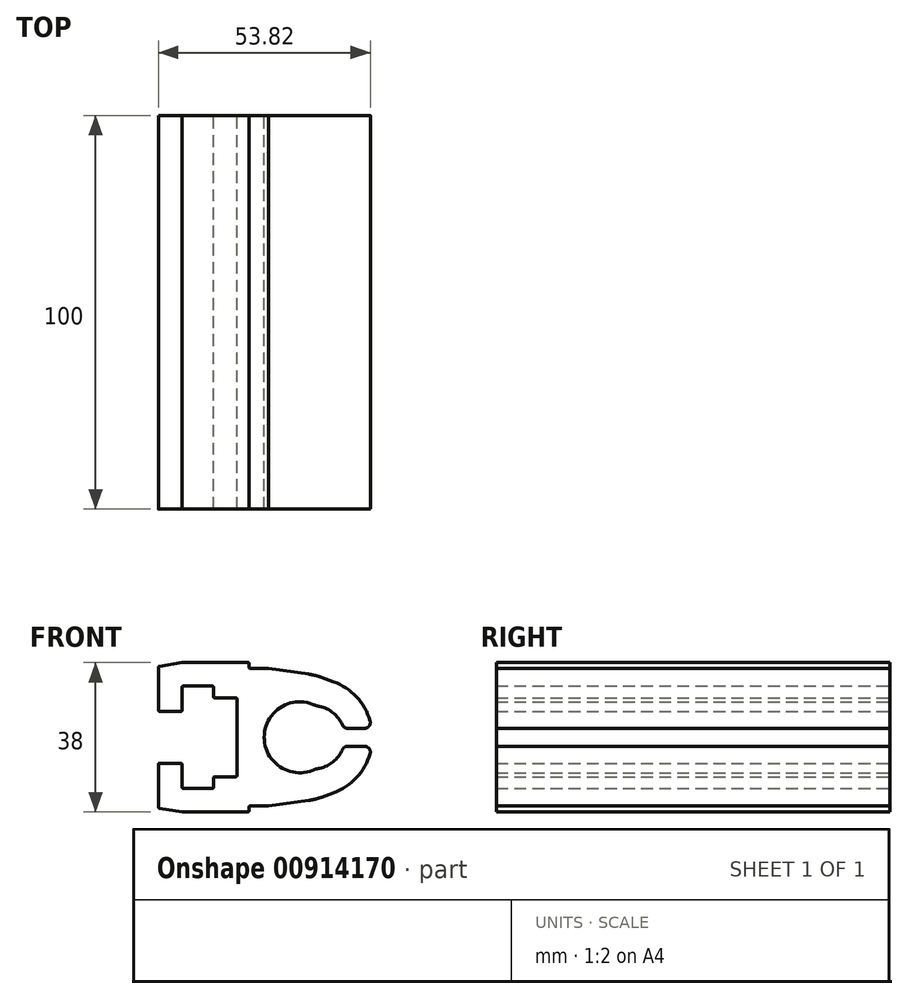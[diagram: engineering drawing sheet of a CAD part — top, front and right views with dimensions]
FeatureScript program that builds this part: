
annotation { "Feature Type Name" : "Feature", "Feature Type Description" : "" }
export const myFeature = defineFeature(function(context is Context, id is Id, definition is map)
    precondition{}
    {
        {
            var Q0;
            Q0=qCreatedBy(makeId("Front.planeOp"),FACE);
            var sketch = newSketch(context, id + "F0", { "sketchPlane" : qUnion([Q0])});
            skLineSegment(sketch, "E0", {"start": v(57.08, -14.1) * mm, "end": v(54, -15.22) * mm});
            skArc(sketch, "E1", {"start": v(50.71, -16.04) * mm, "mid": v(52.37, -15.72) * mm, "end": v(54, -15.22) * mm});
            skLineSegment(sketch, "E2", {"start": v(50.71, -16.04) * mm, "end": v(40.59, -17.47) * mm});
            skLineSegment(sketch, "E3", {"start": v(40.59, -17.47) * mm, "end": v(35.89, -17.47) * mm});
            skArc(sketch, "E4", {"start": v(35.89, -17.47) * mm, "mid": v(35.67, -17.55) * mm, "end": v(35.59, -17.77) * mm});
            skLineSegment(sketch, "E5", {"start": v(35.59, -17.77) * mm, "end": v(35.59, -18.7) * mm});
            skArc(sketch, "E6", {"start": v(35.29, -19) * mm, "mid": v(35.5, -18.91) * mm, "end": v(35.59, -18.7) * mm});
            skLineSegment(sketch, "E7", {"start": v(35.29, -19) * mm, "end": v(18.59, -19) * mm});
            skLineSegment(sketch, "E8", {"start": v(18.59, -19) * mm, "end": v(12.84, -18.04) * mm});
            skArc(sketch, "E9", {"start": v(12.59, -17.75) * mm, "mid": v(12.66, -17.94) * mm, "end": v(12.84, -18.04) * mm});
            skLineSegment(sketch, "E10", {"start": v(12.59, -17.75) * mm, "end": v(12.59, -6.87) * mm});
            skArc(sketch, "E11", {"start": v(12.89, -6.58) * mm, "mid": v(12.67, -6.66) * mm, "end": v(12.59, -6.88) * mm});
            skLineSegment(sketch, "E12", {"start": v(12.89, -6.58) * mm, "end": v(18.29, -6.58) * mm});
            skArc(sketch, "E13", {"start": v(18.59, -6.88) * mm, "mid": v(18.5, -6.66) * mm, "end": v(18.29, -6.58) * mm});
            skLineSegment(sketch, "E14", {"start": v(18.59, -6.88) * mm, "end": v(18.59, -12.7) * mm});
            skArc(sketch, "E15", {"start": v(18.59, -12.7) * mm, "mid": v(18.67, -12.91) * mm, "end": v(18.89, -13) * mm});
            skLineSegment(sketch, "E16", {"start": v(18.89, -13) * mm, "end": v(26.29, -13) * mm});
            skArc(sketch, "E17", {"start": v(26.29, -13) * mm, "mid": v(26.5, -12.91) * mm, "end": v(26.59, -12.7) * mm});
            skLineSegment(sketch, "E18", {"start": v(26.59, -12.7) * mm, "end": v(26.59, -10.3) * mm});
            skArc(sketch, "E19", {"start": v(26.89, -10) * mm, "mid": v(26.67, -10.09) * mm, "end": v(26.59, -10.3) * mm});
            skLineSegment(sketch, "E20", {"start": v(26.89, -10) * mm, "end": v(32.29, -10) * mm});
            skArc(sketch, "E21", {"start": v(32.29, -10) * mm, "mid": v(32.5, -9.91) * mm, "end": v(32.59, -9.7) * mm});
            skLineSegment(sketch, "E22", {"start": v(32.59, -9.7) * mm, "end": v(32.59, 9.7) * mm});
            skArc(sketch, "E23", {"start": v(32.59, 9.7) * mm, "mid": v(32.5, 9.91) * mm, "end": v(32.29, 10) * mm});
            skLineSegment(sketch, "E24", {"start": v(32.29, 10) * mm, "end": v(26.89, 10) * mm});
            skArc(sketch, "E25", {"start": v(26.59, 10.3) * mm, "mid": v(26.67, 10.09) * mm, "end": v(26.89, 10) * mm});
            skLineSegment(sketch, "E26", {"start": v(26.59, 10.3) * mm, "end": v(26.59, 12.7) * mm});
            skArc(sketch, "E27", {"start": v(26.59, 12.7) * mm, "mid": v(26.5, 12.91) * mm, "end": v(26.29, 13) * mm});
            skLineSegment(sketch, "E28", {"start": v(26.29, 13) * mm, "end": v(18.89, 13) * mm});
            skArc(sketch, "E29", {"start": v(18.89, 13) * mm, "mid": v(18.67, 12.91) * mm, "end": v(18.59, 12.7) * mm});
            skLineSegment(sketch, "E30", {"start": v(18.59, 12.7) * mm, "end": v(18.59, 6.88) * mm});
            skArc(sketch, "E31", {"start": v(18.29, 6.58) * mm, "mid": v(18.5, 6.66) * mm, "end": v(18.59, 6.88) * mm});
            skLineSegment(sketch, "E32", {"start": v(18.29, 6.57) * mm, "end": v(12.89, 6.57) * mm});
            skArc(sketch, "E33", {"start": v(12.59, 6.88) * mm, "mid": v(12.67, 6.66) * mm, "end": v(12.89, 6.58) * mm});
            skLineSegment(sketch, "E34", {"start": v(12.59, 6.88) * mm, "end": v(12.59, 17.75) * mm});
            skArc(sketch, "E35", {"start": v(12.84, 18.04) * mm, "mid": v(12.66, 17.94) * mm, "end": v(12.59, 17.75) * mm});
            skLineSegment(sketch, "E36", {"start": v(12.84, 18.04) * mm, "end": v(18.59, 19) * mm});
            skLineSegment(sketch, "E37", {"start": v(18.59, 19) * mm, "end": v(35.29, 19) * mm});
            skArc(sketch, "E38", {"start": v(35.59, 18.7) * mm, "mid": v(35.5, 18.91) * mm, "end": v(35.29, 19) * mm});
            skLineSegment(sketch, "E39", {"start": v(35.59, 18.7) * mm, "end": v(35.59, 17.76) * mm});
            skArc(sketch, "E40", {"start": v(35.59, 17.76) * mm, "mid": v(35.67, 17.55) * mm, "end": v(35.89, 17.46) * mm});
            skLineSegment(sketch, "E41", {"start": v(35.89, 17.46) * mm, "end": v(40.59, 17.46) * mm});
            skLineSegment(sketch, "E42", {"start": v(40.59, 17.46) * mm, "end": v(50.71, 16.04) * mm});
            skArc(sketch, "E43", {"start": v(54, 15.22) * mm, "mid": v(52.37, 15.72) * mm, "end": v(50.71, 16.04) * mm});
            skLineSegment(sketch, "E44", {"start": v(54, 15.22) * mm, "end": v(57.08, 14.1) * mm});
            skArc(sketch, "E45", {"start": v(66.35, 4.2) * mm, "mid": v(62.9, 10.25) * mm, "end": v(57.08, 14.1) * mm});
            skArc(sketch, "E46", {"start": v(64.91, 2.27) * mm, "mid": v(66.11, 2.87) * mm, "end": v(66.35, 4.2) * mm});
            skLineSegment(sketch, "E47", {"start": v(64.91, 2.27) * mm, "end": v(60.67, 2.27) * mm});
            skArc(sketch, "E48", {"start": v(59.3, 3.18) * mm, "mid": v(59.85, 2.52) * mm, "end": v(60.67, 2.27) * mm});
            skArc(sketch, "E49", {"start": v(59.3, 3.18) * mm, "mid": v(56.98, 6.22) * mm, "end": v(53.52, 7.84) * mm});
            skArc(sketch, "E50", {"start": v(51.79, 8.36) * mm, "mid": v(52.64, 8.06) * mm, "end": v(53.52, 7.84) * mm});
            skArc(sketch, "E51", {"start": v(51.79, 8.36) * mm, "mid": v(39.45, 0) * mm, "end": v(51.79, -8.36) * mm});
            skArc(sketch, "E52", {"start": v(53.52, -7.84) * mm, "mid": v(52.64, -8.06) * mm, "end": v(51.79, -8.36) * mm});
            skArc(sketch, "E53", {"start": v(53.52, -7.84) * mm, "mid": v(56.98, -6.22) * mm, "end": v(59.3, -3.18) * mm});
            skArc(sketch, "E54", {"start": v(60.67, -2.28) * mm, "mid": v(59.85, -2.52) * mm, "end": v(59.3, -3.18) * mm});
            skLineSegment(sketch, "E55", {"start": v(60.67, -2.28) * mm, "end": v(64.91, -2.28) * mm});
            skArc(sketch, "E56", {"start": v(66.35, -4.2) * mm, "mid": v(66.11, -2.87) * mm, "end": v(64.91, -2.28) * mm});
            skArc(sketch, "E57", {"start": v(57.08, -14.1) * mm, "mid": v(62.9, -10.25) * mm, "end": v(66.35, -4.2) * mm});
            skSolve(sketch);
        }
        {
            var Q0;
            Q0=makeQuery(id+"F0.imprint","IMPRINT",FACE,{"disambiguationData":[TD([[makeQuery(id+"F0.imprint","IMPRINT",EDGE,{"derivedFrom":sQuery(id+"F0.wireOp",EDGE,"E0")}),-1.0]])]});
            extrude(context, id + "F1", {"entities" : qUnion([Q0]), "endBound" : BoundingType.SYMMETRIC, "depth" : 100 * mm, "offsetDistance" : 25 * mm});
        }
    });
